# Revit family: O88621001_Orinal Entrada Superior
name_source: partatom
category: Plumbing Fixtures
units: mm (PartAtom-declared; Revit-internal decimal feet)

## family parameters
Always vertical = Yes
Cut with Voids When Loaded = No
Host = Wall
OmniClass Number = 23.31.21.00
OmniClass Title = Urinals
Part Type = Normal
Room Calculation Point = No
Round Connector Dimension = Use Diameter
Shared = No

## types (1)
- Type 1
    Alto = 430 mm
    Ancho = 300 mm  [stored 0.984252 ft]
    Consumo de Agua = 3.8 Lpf (1.0 gpf)
    Creado por = BIMBAU
    Default Elevation = 0 mm  [stored 0 ft]
    Description = Conoce ahora mismo nuestro orinal Mediano con diseño compacto y de formas redondeadas. Un producto perfecto para espacios pequeños y de bajo tráfico.
    Fecha de creación = 12/03/2021
    Garantía = Integral de por vida
    Manufacturer = Corona
    Material = Corona_Porcelana_Sanitaria
    Material 2 = Corona_Acero
    Model = Orinal Mediano entrada superior
    Peso del Producto Empacado = 17.4 lb (7.9 kg)
    Profundidad = 300 mm  [stored 0.984252 ft]
    Racor de Entrada de Agua. = 1.27 cm (1/2) - 1.88 (3/4)
    Racor de Salida = 2.54cm (1)
    Rango de Presión de Agua = 25 a 125 PSI (Varía Según la grifería )
    Referencia = O88621001
    URL = https://corona.co

note: [stored X ft] marks values corroborated as IEEE doubles in the binary element streams (Revit-internal decimal feet)

## geometry (parser evidence)
native form markers: Sweep x5
no freeform markers — native parametric forms only
